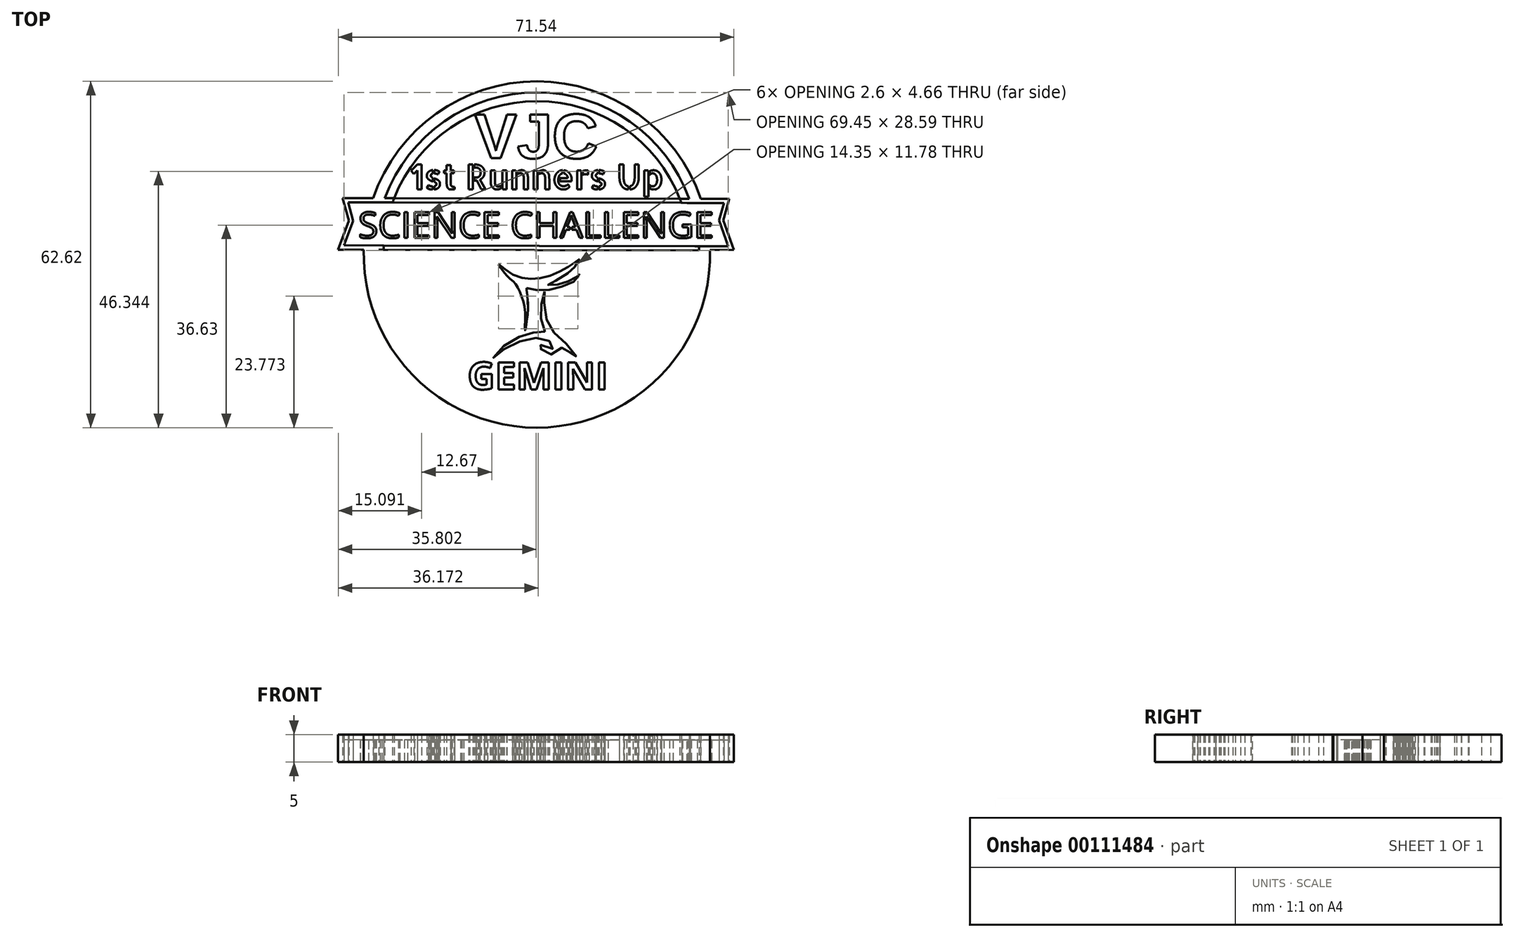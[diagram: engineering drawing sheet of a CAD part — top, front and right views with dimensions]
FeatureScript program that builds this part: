
annotation { "Feature Type Name" : "Feature", "Feature Type Description" : "" }
export const myFeature = defineFeature(function(context is Context, id is Id, definition is map)
    precondition{}
    {
        {
            var Q0;
            Q0=qCreatedBy(makeId("Top.planeOp"),FACE);
            var sketch = newSketch(context, id + "F0", { "sketchPlane" : qUnion([Q0])});
            skCircle(sketch, "E0", {"center": v(0.94, -3) * mm, "radius": 27.74 * mm});
            skPoint(sketch, "E0.first.point", {"position": v(1.58, 24.74) * mm});
            skPoint(sketch, "E0.second.point", {"position": v(0.52, -30.73) * mm});
            skPoint(sketch, "E0.third.point", {"position": v(-26.76, -1.33) * mm});
            skLineSegment(sketch, "E1", {"start": v(-24.87, 7.2) * mm, "end": v(-34.2, 7.2) * mm});
            skLineSegment(sketch, "E2", {"start": v(-34.2, 7.2) * mm, "end": v(-33.08, 3.11) * mm});
            skLineSegment(sketch, "E3", {"start": v(-33.08, 3.11) * mm, "end": v(-35, -2.1) * mm});
            skLineSegment(sketch, "E4", {"start": v(-35, -2.1) * mm, "end": v(-26.8, -2.1) * mm});
            skLineSegment(sketch, "E5", {"start": v(26.78, 7.1) * mm, "end": v(35.71, 7.1) * mm});
            skLineSegment(sketch, "E6", {"start": v(35.71, 7.1) * mm, "end": v(34.66, 3.21) * mm});
            skLineSegment(sketch, "E7", {"start": v(34.66, 3.21) * mm, "end": v(36.55, -2.1) * mm});
            skLineSegment(sketch, "E8", {"start": v(36.55, -2.1) * mm, "end": v(28.67, -2.25) * mm});
            skFitSpline(sketch, "E9", {"points": [v(-6, -4.72) * mm, v(-5.23, -5.35) * mm, v(-3.9, -6.35) * mm, v(-2.48, -6.98) * mm, v(-0.85, -7.35) * mm, v(0.35, -7.37) * mm, v(2.08, -7.15) * mm, v(3.86, -6.6) * mm, v(5.5, -5.84) * mm, v(6.83, -5.05) * mm, v(7.95, -4.34) * mm, v(8.2, -4.17) * mm, v(8.54, -3.89) * mm, v(8.14, -4.78) * mm, v(7.2, -5.82) * mm, v(5.2, -7.28) * mm, v(2.9, -8.45) * mm, v(3.98, -8.47) * mm, v(5.87, -8.12) * mm, v(7.76, -7.26) * mm, v(8.43, -6.75) * mm, v(8.6, -6.46) * mm, v(8.47, -7.15) * mm, v(6.46, -8.4) * mm, v(3.8, -9.28) * mm, v(1.11, -9.42) * mm, v(-0.95, -9.06) * mm], "startDerivative": vector(22.31, -18.25) * mm, "endDerivative": vector(-43, 9.84) * mm});
            skFitSpline(sketch, "E10", {"points": [v(-6, -4.72) * mm, v(-5.19, -6.01) * mm, v(-3.81, -7.48) * mm, v(-3.02, -8.2) * mm, v(-2.26, -9.47) * mm, v(-1.53, -11.45) * mm, v(-1.17, -13.95) * mm, v(-1.2, -16.67) * mm, v(-0.95, -15.45) * mm, v(-0.68, -11.98) * mm, v(-0.91, -9.36) * mm, v(-0.95, -9.06) * mm], "startDerivative": vector(8.3, -15) * mm, "endDerivative": vector(-0.86, 6) * mm});
            skFitSpline(sketch, "E11", {"points": [v(2.34, -9.66) * mm, v(2.02, -10.62) * mm, v(1.67, -12.76) * mm, v(1.67, -14.3) * mm, v(2.06, -16.19) * mm, v(2.36, -16.95) * mm, v(1.82, -16.92) * mm, v(-0.01, -17.17) * mm, v(-1.66, -17.64) * mm, v(-3.97, -18.79) * mm, v(-6.02, -20.44) * mm, v(-6.96, -21.68) * mm, v(-5.91, -20.77) * mm, v(-3.67, -19.33) * mm, v(-1.3, -18.4) * mm, v(0.83, -18.07) * mm, v(2.42, -18.3) * mm, v(3.7, -19.03) * mm, v(4.04, -19.68) * mm, v(3.45, -20.21) * mm, v(1.98, -19.81) * mm, v(1.3, -18.87) * mm, v(1.45, -19.8) * mm, v(2.36, -20.56) * mm, v(3.3, -21.02) * mm, v(4.84, -20.7) * mm, v(5.53, -19.8) * mm, v(6.38, -20.28) * mm, v(7.16, -20.84) * mm, v(8.14, -21.87) * mm, v(7.64, -20.68) * mm, v(6.28, -19.14) * mm, v(4.5, -17.53) * mm, v(3.33, -16.29) * mm, v(2.56, -14.18) * mm, v(2.24, -11.68) * mm, v(2.33, -10.24) * mm, v(2.34, -9.66) * mm]});
            skLineSegment(sketch, "E12", {"start": v(-24.87, 7.2) * mm, "end": v(28.1, 7.1) * mm});
            skLineSegment(sketch, "E13", {"start": v(-27.68, -2.1) * mm, "end": v(29.48, -2.24) * mm});
            skCircle(sketch, "E14.0", {"center": v(0.94, -3) * mm, "radius": 29.33 * mm});
            skCircle(sketch, "E15.0", {"center": v(0.94, -3) * mm, "radius": 31.31 * mm});
            skLineSegment(sketch, "E16.0", {"start": v(-24.87, 6.45) * mm, "end": v(28.1, 6.35) * mm});
            skLineSegment(sketch, "E17.0", {"start": v(-24.87, 6.45) * mm, "end": v(-33.21, 6.45) * mm});
            skLineSegment(sketch, "E18", {"start": v(28.1, 6.35) * mm, "end": v(34.73, 6.35) * mm});
            skLineSegment(sketch, "E19.0", {"start": v(-27.68, -1.35) * mm, "end": v(29.48, -1.49) * mm});
            skLineSegment(sketch, "E20", {"start": v(-27.68, -1.35) * mm, "end": v(-33.91, -1.33) * mm});
            skLineSegment(sketch, "E21", {"start": v(29.48, -1.49) * mm, "end": v(35.54, -1.5) * mm});
            skLineSegment(sketch, "E22.0", {"start": v(34.73, 6.35) * mm, "end": v(33.88, 3.18) * mm});
            skLineSegment(sketch, "E23.0", {"start": v(33.88, 3.18) * mm, "end": v(35.54, -1.5) * mm});
            skLineSegment(sketch, "E24.0", {"start": v(-32.3, 3.08) * mm, "end": v(-33.91, -1.33) * mm});
            skLineSegment(sketch, "E25.trimOffspring", {"start": v(-33.21, 6.45) * mm, "end": v(-32.3, 3.08) * mm});
            skText(sketch, "E26", { "text": "SCIENCE CHALLENGE", "fontName": "OpenSans-Regular.ttf"});
            skText(sketch, "E27", { "text": "GEMINI", "fontName": "OpenSans-Bold.ttf"});
            skText(sketch, "E28", { "text": "VJC", "fontName": "Arimo-Bold.ttf"});
            skLineSegment(sketch, "E29", {"start": v(6.9, 1.33) * mm, "end": v(6.9, 2.22) * mm});
            skLineSegment(sketch, "E30", {"start": v(6.9, 2.22) * mm, "end": v(7.18, 2.22) * mm});
            skLineSegment(sketch, "E31", {"start": v(7.18, 2.22) * mm, "end": v(7.26, 2.22) * mm});
            skLineSegment(sketch, "E32", {"start": v(7.26, 2.22) * mm, "end": v(7.26, 1.34) * mm});
            skLineSegment(sketch, "E33", {"start": v(7.26, 1.34) * mm, "end": v(6.9, 1.33) * mm});
            skText(sketch, "E34", { "text": "1st Runners Up", "fontName": "AllertaStencil-Regular.ttf"});
            const initialGuessF0  = {"E26": [-0.03136, 0, 1, 0, 0.0047], "E27": [-0.0116, -0.02738, 1, 0, 0.00494], "E28": [-0.01032, 0.01442, 1, 0, 0.00826], "E34": [-0.02198, 0.00879, 1, 0, 0.00449]};
            skSetInitialGuess(sketch, initialGuessF0);
            skSolve(sketch);
        }
        {
            var Q0;
            Q0=makeQuery(id+"F0.imprint","IMPRINT",FACE,{"disambiguationData":[TD([[makeQuery(id+"F0.imprint","IMPRINT",EDGE,{"derivedFrom":sQuery(id+"F0.wireOp",EDGE,"f2c7ee9f-897c-4c1d-89b3-a48ac7c6bfa7.sketch_text.stroke-0")}),1.0]])]});
            var Q1;
            {var subQ0=sQuery(id+"F0.wireOp",EDGE,"E15.0");var subQ1=sQuery(id+"F0.wireOp",EDGE,"E1");var subQ2=makeQuery(id+"F0.imprint","INTERSECT",VERTEX,{"derivedFrom":[subQ1,subQ0]});Q1=makeQuery(id+"F0.imprint","IMPRINT",FACE,{"disambiguationData":[TD([[makeQuery(id+"F0.imprint","IMPRINT",EDGE,{"disambiguationData":[TD([[subQ2,1.0]])],"derivedFrom":subQ1}),-1.0]])]});}
            var Q2;
            Q2=makeQuery(id+"F0.imprint","IMPRINT",FACE,{"disambiguationData":[TD([[makeQuery(id+"F0.imprint","IMPRINT",EDGE,{"derivedFrom":sQuery(id+"F0.wireOp",EDGE,"26462852-2f77-49b2-9a3d-6dfd93b606f1.sketch_text.stroke-0")}),1.0]])]});
            var Q3;
            {var subQ0=sQuery(id+"F0.wireOp",EDGE,"E15.0");var subQ1=sQuery(id+"F0.wireOp",EDGE,"E4");var subQ2=makeQuery(id+"F0.imprint","INTERSECT",VERTEX,{"derivedFrom":[subQ1,subQ0]});Q3=makeQuery(id+"F0.imprint","IMPRINT",FACE,{"disambiguationData":[TD([[makeQuery(id+"F0.imprint","IMPRINT",EDGE,{"disambiguationData":[TD([[subQ2,-1.0]])],"derivedFrom":subQ1}),-1.0]])]});}
            var Q4;
            {var subQ7=sQuery(id+"F0.wireOp",EDGE,"E2");Q4=makeQuery(id+"F0.imprint","IMPRINT",FACE,{"disambiguationData":[TD([[makeQuery(id+"F0.imprint","IMPRINT",EDGE,{"derivedFrom":subQ7}),1.0]])]});}
            var Q5;
            {var subQ3=sQuery(id+"F0.wireOp",EDGE,"E17.0");var subQ10=makeQuery(id+"F0.imprint","IMPRINT",VERTEX,{"derivedFrom":subQ3});Q5=makeQuery(id+"F0.imprint","IMPRINT",FACE,{"disambiguationData":[TD([[makeQuery(id+"F0.imprint","IMPRINT",EDGE,{"disambiguationData":[TD([[subQ10,1.0]])],"derivedFrom":subQ3}),-1.0]])]});}
            var Q6;
            {var subQ0=sQuery(id+"F0.wireOp",EDGE,"E1");var subQ5=sQuery(id+"F0.wireOp",EDGE,"E14.0");var subQ6=makeQuery(id+"F0.imprint","INTERSECT",VERTEX,{"derivedFrom":[subQ0,subQ5]});Q6=makeQuery(id+"F0.imprint","IMPRINT",FACE,{"disambiguationData":[TD([[makeQuery(id+"F0.imprint","IMPRINT",EDGE,{"disambiguationData":[TD([[subQ6,-1.0]])],"derivedFrom":subQ5}),1.0]])]});}
            var Q7;
            {var subQ1=sQuery(id+"F0.wireOp",EDGE,"E5");var subQ6=sQuery(id+"F0.wireOp",EDGE,"E0");var subQ7=makeQuery(id+"F0.imprint","INTERSECT",VERTEX,{"derivedFrom":[subQ6,subQ1]});Q7=makeQuery(id+"F0.imprint","IMPRINT",FACE,{"disambiguationData":[TD([[makeQuery(id+"F0.imprint","IMPRINT",EDGE,{"disambiguationData":[TD([[subQ7,1.0]])],"derivedFrom":subQ6}),-1.0]])]});}
            var Q8;
            {var subQ0=sQuery(id+"F0.wireOp",EDGE,"E15.0");var subQ1=sQuery(id+"F0.wireOp",EDGE,"E5");var subQ2=makeQuery(id+"F0.imprint","INTERSECT",VERTEX,{"derivedFrom":[subQ1,subQ0]});Q8=makeQuery(id+"F0.imprint","IMPRINT",FACE,{"disambiguationData":[TD([[makeQuery(id+"F0.imprint","IMPRINT",EDGE,{"disambiguationData":[TD([[subQ2,1.0]])],"derivedFrom":subQ1}),-1.0]])]});}
            var Q9;
            {var subQ11=sQuery(id+"F0.wireOp",EDGE,"E6");Q9=makeQuery(id+"F0.imprint","IMPRINT",FACE,{"disambiguationData":[TD([[makeQuery(id+"F0.imprint","IMPRINT",EDGE,{"derivedFrom":subQ11}),-1.0]])]});}
            var Q10;
            {var subQ0=sQuery(id+"F0.wireOp",EDGE,"E13");var subQ1=sQuery(id+"F0.wireOp",EDGE,"E0");var subQ2=makeQuery(id+"F0.imprint","INTERSECT",VERTEX,{"disambiguationData":[OD(0.0)],"derivedFrom":[subQ1,subQ0]});Q10=makeQuery(id+"F0.imprint","IMPRINT",FACE,{"disambiguationData":[TD([[makeQuery(id+"F0.imprint","IMPRINT",EDGE,{"disambiguationData":[TD([[subQ2,-1.0]])],"derivedFrom":subQ1}),1.0]])]});}
            var Q11;
            {var subQ0=sQuery(id+"F0.wireOp",EDGE,"E13");var subQ3=sQuery(id+"F0.wireOp",EDGE,"E0");var subQ4=makeQuery(id+"F0.imprint","INTERSECT",VERTEX,{"disambiguationData":[OD(0.0)],"derivedFrom":[subQ3,subQ0]});Q11=makeQuery(id+"F0.imprint","IMPRINT",FACE,{"disambiguationData":[TD([[makeQuery(id+"F0.imprint","IMPRINT",EDGE,{"disambiguationData":[TD([[subQ4,-1.0]])],"derivedFrom":subQ3}),-1.0]])]});}
            var Q12;
            {var subQ0=sQuery(id+"F0.wireOp",EDGE,"E15.0");var subQ1=sQuery(id+"F0.wireOp",EDGE,"E8");var subQ2=makeQuery(id+"F0.imprint","INTERSECT",VERTEX,{"derivedFrom":[subQ1,subQ0]});Q12=makeQuery(id+"F0.imprint","IMPRINT",FACE,{"disambiguationData":[TD([[makeQuery(id+"F0.imprint","IMPRINT",EDGE,{"disambiguationData":[TD([[subQ2,-1.0]])],"derivedFrom":subQ1}),-1.0]])]});}
            var Q13;
            {var subQ0=sQuery(id+"F0.wireOp",EDGE,"E15.0");var subQ1=sQuery(id+"F0.wireOp",EDGE,"E1");var subQ2=makeQuery(id+"F0.imprint","INTERSECT",VERTEX,{"derivedFrom":[subQ1,subQ0]});Q13=makeQuery(id+"F0.imprint","IMPRINT",FACE,{"disambiguationData":[TD([[makeQuery(id+"F0.imprint","IMPRINT",EDGE,{"disambiguationData":[TD([[subQ2,1.0]])],"derivedFrom":subQ1}),1.0]])]});}
            var Q14;
            {var subQ0=sQuery(id+"F0.wireOp",EDGE,"E15.0");var subQ1=sQuery(id+"F0.wireOp",EDGE,"E4");var subQ2=makeQuery(id+"F0.imprint","INTERSECT",VERTEX,{"derivedFrom":[subQ1,subQ0]});Q14=makeQuery(id+"F0.imprint","IMPRINT",FACE,{"disambiguationData":[TD([[makeQuery(id+"F0.imprint","IMPRINT",EDGE,{"disambiguationData":[TD([[subQ2,-1.0]])],"derivedFrom":subQ1}),1.0]])]});}
            var Q15;
            {var subQ0=sQuery(id+"F0.wireOp",EDGE,"E4");var subQ1=sQuery(id+"F0.wireOp",EDGE,"E0");var subQ2=makeQuery(id+"F0.imprint","INTERSECT",VERTEX,{"derivedFrom":[subQ1,subQ0]});Q15=makeQuery(id+"F0.imprint","IMPRINT",FACE,{"disambiguationData":[TD([[makeQuery(id+"F0.imprint","IMPRINT",EDGE,{"disambiguationData":[TD([[subQ2,1.0]])],"derivedFrom":subQ1}),-1.0]])]});}
            var Q16;
            Q16=makeQuery(id+"F0.imprint","IMPRINT",FACE,{"disambiguationData":[TD([[makeQuery(id+"F0.imprint","IMPRINT",EDGE,{"derivedFrom":sQuery(id+"F0.wireOp",EDGE,"E9")}),1.0]])]});
            var Q17;
            Q17=makeQuery(id+"F0.imprint","IMPRINT",FACE,{"disambiguationData":[TD([[makeQuery(id+"F0.imprint","IMPRINT",EDGE,{"derivedFrom":sQuery(id+"F0.wireOp",EDGE,"E28.sketch_text.stroke-0")}),1.0]])]});
            extrude(context, id + "F1", {"entities" : qUnion([Q0, Q1, Q2, Q3, Q4, Q5, Q6, Q7, Q8, Q9, Q10, Q11, Q12, Q13, Q14, Q15, Q16, Q17]), "depth" : 5 * mm});
        }
        {
            var Q0;
            {var subQ0=sQuery(id+"F0.wireOp",EDGE,"E24.0");Q0=makeQuery(id+"F0.imprint","IMPRINT",FACE,{"disambiguationData":[TD([[makeQuery(id+"F0.imprint","IMPRINT",EDGE,{"derivedFrom":subQ0}),1.0]])]});}
            var Q1;
            {var subQ11=sQuery(id+"F0.wireOp",EDGE,"E26.sketch_text.stroke-16");Q1=makeQuery(id+"F0.imprint","IMPRINT",FACE,{"disambiguationData":[TD([[makeQuery(id+"F0.imprint","IMPRINT",EDGE,{"derivedFrom":subQ11}),1.0]])]});}
            var Q2;
            {var subQ0=sQuery(id+"F0.wireOp",EDGE,"E26.sketch_text.stroke-33");Q2=makeQuery(id+"F0.imprint","IMPRINT",FACE,{"disambiguationData":[TD([[makeQuery(id+"F0.imprint","IMPRINT",EDGE,{"derivedFrom":subQ0}),1.0]])]});}
            var Q3;
            {var subQ10=sQuery(id+"F0.wireOp",EDGE,"E26.sketch_text.stroke-28");Q3=makeQuery(id+"F0.imprint","IMPRINT",FACE,{"disambiguationData":[TD([[makeQuery(id+"F0.imprint","IMPRINT",EDGE,{"derivedFrom":subQ10}),1.0]])]});}
            var Q4;
            {var subQ25=sQuery(id+"F0.wireOp",EDGE,"E26.sketch_text.stroke-178");Q4=makeQuery(id+"F0.imprint","IMPRINT",FACE,{"disambiguationData":[TD([[makeQuery(id+"F0.imprint","IMPRINT",EDGE,{"derivedFrom":subQ25}),1.0]])]});}
            var Q5;
            {var subQ1=sQuery(id+"F0.wireOp",EDGE,"E26.sketch_text.stroke-198");var subQ3=sQuery(id+"F0.wireOp",EDGE,"E14.0");var subQ4=makeQuery(id+"F0.imprint","INTERSECT",VERTEX,{"derivedFrom":[subQ3,subQ1]});Q5=makeQuery(id+"F0.imprint","IMPRINT",FACE,{"disambiguationData":[TD([[makeQuery(id+"F0.imprint","IMPRINT",EDGE,{"disambiguationData":[TD([[subQ4,-1.0]])],"derivedFrom":subQ3}),-1.0]])]});}
            var Q6;
            {var subQ8=sQuery(id+"F0.wireOp",EDGE,"E22.0");Q6=makeQuery(id+"F0.imprint","IMPRINT",FACE,{"disambiguationData":[TD([[makeQuery(id+"F0.imprint","IMPRINT",EDGE,{"derivedFrom":subQ8}),-1.0]])]});}
            var Q7;
            {var subQ0=sQuery(id+"F0.wireOp",EDGE,"E26.sketch_text.stroke-6");Q7=makeQuery(id+"F0.imprint","IMPRINT",FACE,{"disambiguationData":[TD([[makeQuery(id+"F0.imprint","IMPRINT",EDGE,{"derivedFrom":subQ0}),1.0]])]});}
            var Q8;
            {var subQ6=sQuery(id+"F0.wireOp",EDGE,"E26.sketch_text.stroke-1");Q8=makeQuery(id+"F0.imprint","IMPRINT",FACE,{"disambiguationData":[TD([[makeQuery(id+"F0.imprint","IMPRINT",EDGE,{"derivedFrom":subQ6}),1.0]])]});}
            var Q9;
            {var subQ6=sQuery(id+"F0.wireOp",EDGE,"E26.sketch_text.stroke-189");Q9=makeQuery(id+"F0.imprint","IMPRINT",FACE,{"disambiguationData":[TD([[makeQuery(id+"F0.imprint","IMPRINT",EDGE,{"derivedFrom":subQ6}),1.0]])]});}
            var Q10;
            {var subQ5=sQuery(id+"F0.wireOp",EDGE,"E26.sketch_text.stroke-202");Q10=makeQuery(id+"F0.imprint","IMPRINT",FACE,{"disambiguationData":[TD([[makeQuery(id+"F0.imprint","IMPRINT",EDGE,{"derivedFrom":subQ5}),1.0]])]});}
            var Q11;
            {var subQ5=sQuery(id+"F0.wireOp",EDGE,"E26.sketch_text.stroke-206");Q11=makeQuery(id+"F0.imprint","IMPRINT",FACE,{"disambiguationData":[TD([[makeQuery(id+"F0.imprint","IMPRINT",EDGE,{"derivedFrom":subQ5}),1.0]])]});}
            var Q12;
            {var subQ0=sQuery(id+"F0.wireOp",EDGE,"E21");var subQ1=sQuery(id+"F0.wireOp",EDGE,"E14.0");var subQ2=makeQuery(id+"F0.imprint","INTERSECT",VERTEX,{"derivedFrom":[subQ1,subQ0]});Q12=makeQuery(id+"F0.imprint","IMPRINT",FACE,{"disambiguationData":[TD([[makeQuery(id+"F0.imprint","IMPRINT",EDGE,{"disambiguationData":[TD([[subQ2,-1.0]])],"derivedFrom":subQ1}),-1.0]])]});}
            var Q13;
            Q13=makeQuery(id+"F0.imprint","IMPRINT",FACE,{"disambiguationData":[TD([[makeQuery(id+"F0.imprint","IMPRINT",EDGE,{"derivedFrom":sQuery(id+"F0.wireOp",EDGE,"E26.sketch_text.stroke-133")}),1.0]])]});
            var Q14;
            {var subQ5=sQuery(id+"F0.wireOp",EDGE,"E26.sketch_text.stroke-26");Q14=makeQuery(id+"F0.imprint","IMPRINT",FACE,{"disambiguationData":[TD([[makeQuery(id+"F0.imprint","IMPRINT",EDGE,{"derivedFrom":subQ5}),1.0]])]});}
            var Q15;
            {var subQ1=sQuery(id+"F0.wireOp",EDGE,"E26.sketch_text.stroke-19");Q15=makeQuery(id+"F0.imprint","IMPRINT",FACE,{"disambiguationData":[TD([[makeQuery(id+"F0.imprint","IMPRINT",EDGE,{"derivedFrom":subQ1}),1.0]])]});}
            var Q16;
            {var subQ5=sQuery(id+"F0.wireOp",EDGE,"E33");Q16=makeQuery(id+"F0.imprint","IMPRINT",FACE,{"disambiguationData":[TD([[makeQuery(id+"F0.imprint","IMPRINT",EDGE,{"derivedFrom":subQ5}),-1.0]])]});}
            var Q17;
            {var subQ0=sQuery(id+"F0.wireOp",EDGE,"E32");var subQ1=sQuery(id+"F0.wireOp",EDGE,"E26.sketch_text.stroke-126");var subQ2=makeQuery(id+"F0.imprint","INTERSECT",VERTEX,{"derivedFrom":[subQ1,subQ0]});Q17=makeQuery(id+"F0.imprint","IMPRINT",FACE,{"disambiguationData":[TD([[makeQuery(id+"F0.imprint","IMPRINT",EDGE,{"disambiguationData":[TD([[subQ2,-1.0]])],"derivedFrom":subQ1}),-1.0]])]});}
            var Q18;
            {var subQ1=sQuery(id+"F0.wireOp",EDGE,"E30");Q18=makeQuery(id+"F0.imprint","IMPRINT",FACE,{"disambiguationData":[TD([[makeQuery(id+"F0.imprint","IMPRINT",EDGE,{"derivedFrom":subQ1}),-1.0]])]});}
            extrude(context, id + "F2", {"entities" : qUnion([Q0, Q1, Q2, Q3, Q4, Q5, Q6, Q7, Q8, Q9, Q10, Q11, Q12, Q13, Q14, Q15, Q16, Q17, Q18]), "depth" : 4 * mm});
        }
    });
